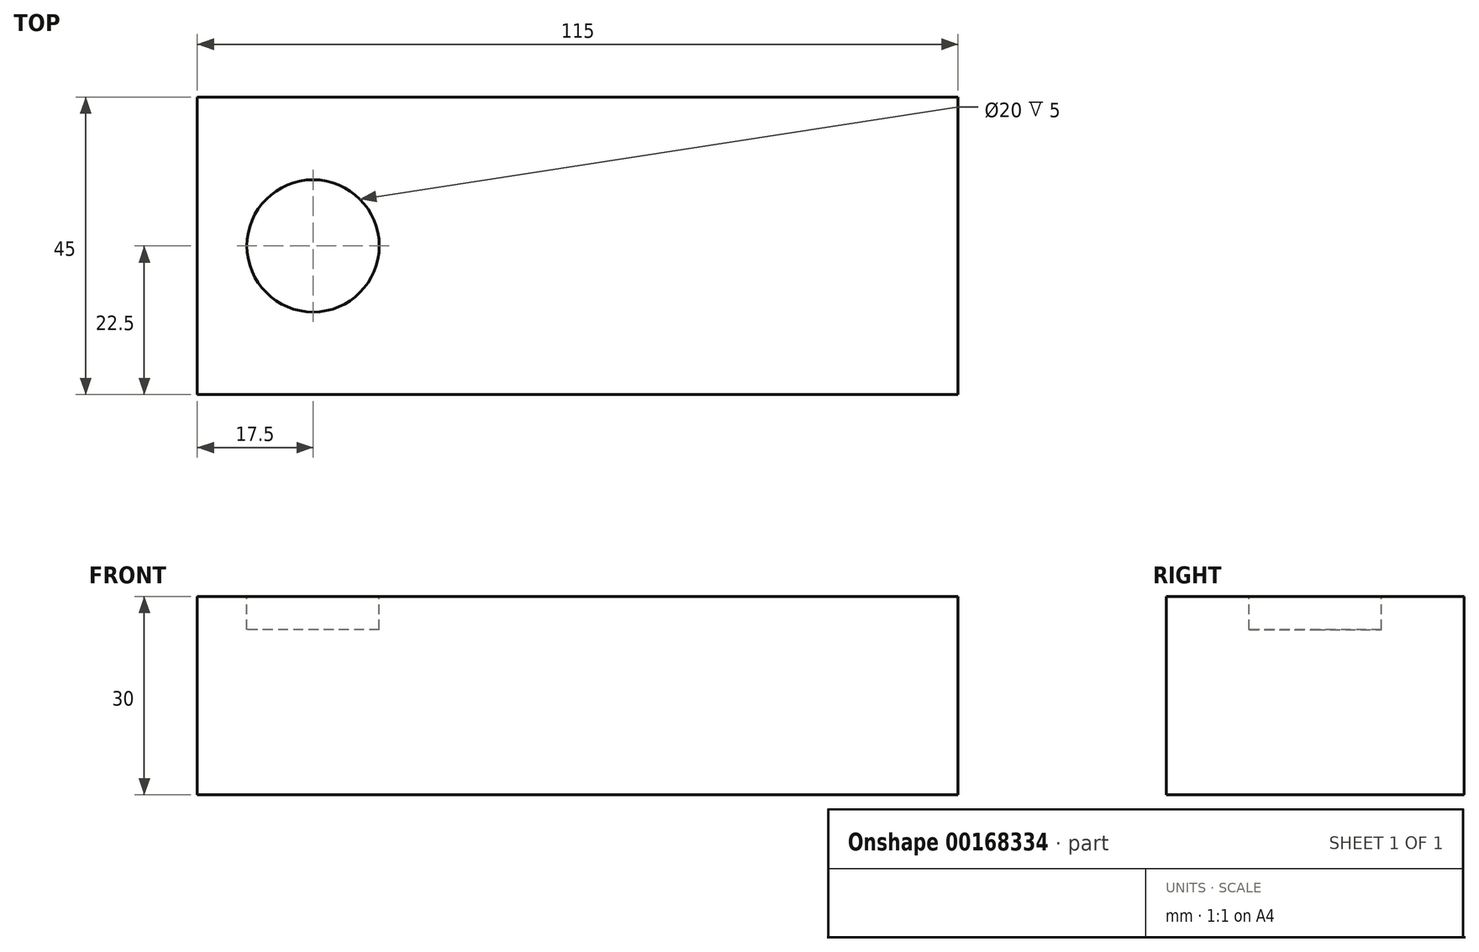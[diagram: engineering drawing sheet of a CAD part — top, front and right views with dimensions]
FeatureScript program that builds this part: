
annotation { "Feature Type Name" : "Feature", "Feature Type Description" : "" }
export const myFeature = defineFeature(function(context is Context, id is Id, definition is map)
    precondition{}
    {
        {
            var Q0;
            Q0=qCreatedBy(makeId("Top.planeOp"),FACE);
            var sketch = newSketch(context, id + "F0", { "sketchPlane" : qUnion([Q0])});
            skLineSegment(sketch, "E0.bottom", {"start": v(-57.5, 22.5) * mm, "end": v(57.5, 22.5) * mm});
            skLineSegment(sketch, "E0.top", {"start": v(-57.5, -22.5) * mm, "end": v(57.5, -22.5) * mm});
            skLineSegment(sketch, "E0.left", {"start": v(-57.5, 22.5) * mm, "end": v(-57.5, -22.5) * mm});
            skLineSegment(sketch, "E0.right", {"start": v(57.5, 22.5) * mm, "end": v(57.5, -22.5) * mm});
            skPoint(sketch, "E0.middle", {"position": v(0, 0) * mm});
            skSolve(sketch);
        }
        {
            var Q0;
            Q0=makeQuery(id+"F0.imprint","IMPRINT",FACE,{"disambiguationData":[TD([[makeQuery(id+"F0.imprint","IMPRINT",EDGE,{"derivedFrom":sQuery(id+"F0.wireOp",EDGE,"E0.bottom")}),-1.0]])]});
            extrude(context, id + "F1", {"entities" : qUnion([Q0]), "depth" : 30 * mm});
        }
        {
            var Q0;
            Q0=makeQuery(id+"F1.opExtrude","CAP_FACE",FACE,{"disambiguationData":[OSD([sQuery(id+"F0.wireOp",EDGE,"E0.bottom"),sQuery(id+"F0.wireOp",EDGE,"E0.top"),sQuery(id+"F0.wireOp",EDGE,"E0.left"),sQuery(id+"F0.wireOp",EDGE,"E0.right")])],"isStart":false});
            var sketch = newSketch(context, id + "F2", { "sketchPlane" : qUnion([Q0])});
            skCircle(sketch, "E1", {"center": v(-40, 0) * mm, "radius": 10 * mm});
            skPoint(sketch, "E1.first.point", {"position": v(-30, 0) * mm});
            skPoint(sketch, "E1.second.point", {"position": v(-46, -8) * mm});
            skPoint(sketch, "E1.third.point", {"position": v(-31.34, -5) * mm});
            skSolve(sketch);
        }
        {
            var Q0;
            Q0=makeQuery(id+"F2.imprint","IMPRINT",FACE,{"disambiguationData":[TD([[makeQuery(id+"F2.imprint","IMPRINT",EDGE,{"derivedFrom":sQuery(id+"F2.wireOp",EDGE,"E1")}),1.0]])]});
            extrude(context, id + "F3", {"entities" : qUnion([Q0]), "operationType" : NewBodyOperationType.REMOVE, "oppositeDirection" : true, "depth" : 5 * mm});
        }
    });
